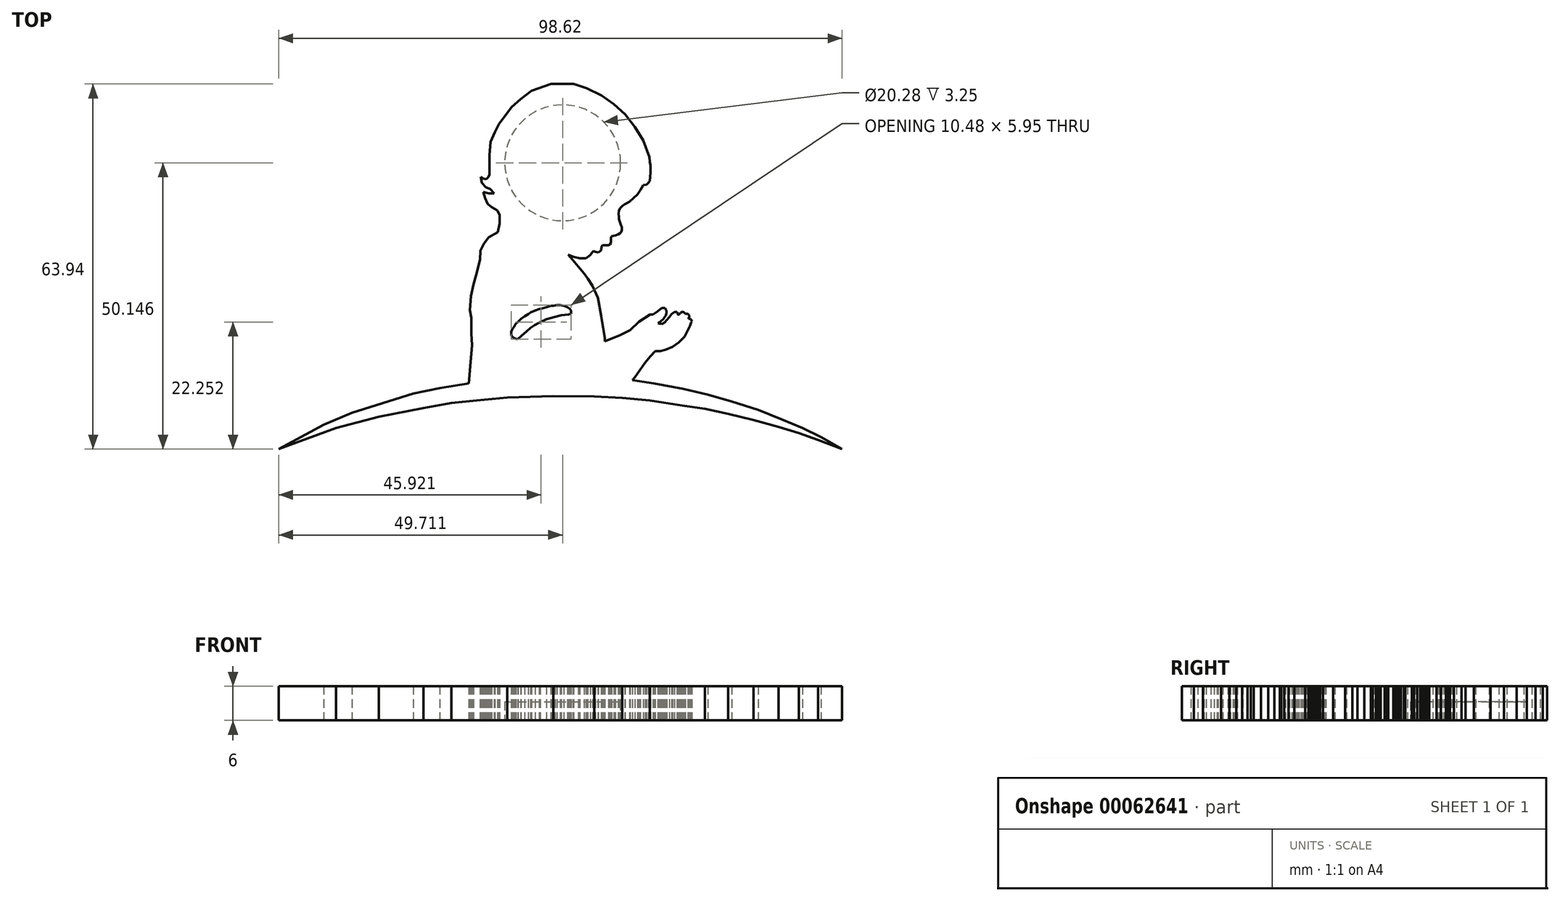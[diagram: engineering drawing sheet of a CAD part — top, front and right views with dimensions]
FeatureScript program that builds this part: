
annotation { "Feature Type Name" : "Feature", "Feature Type Description" : "" }
export const myFeature = defineFeature(function(context is Context, id is Id, definition is map)
    precondition{}
    {
        {
            var Q0;
            Q0=qCreatedBy(makeId("Top.planeOp"),FACE);
            var sketch = newSketch(context, id + "F0", { "sketchPlane" : qUnion([Q0])});
            skPoint(sketch, "E0", {"position": v(-48.76, -25.75) * mm});
            skPoint(sketch, "E1", {"position": v(-35.94, -19.4) * mm});
            skPoint(sketch, "E2", {"position": v(-15.46, -14.25) * mm});
            skPoint(sketch, "E3", {"position": v(-25.2, -16) * mm});
            skPoint(sketch, "E4", {"position": v(-15.02, -5.48) * mm});
            skPoint(sketch, "E5", {"position": v(-15.02, -2.75) * mm});
            skPoint(sketch, "E6", {"position": v(-13.48, 7.44) * mm});
            skPoint(sketch, "E7", {"position": v(-10.42, 12.26) * mm});
            skPoint(sketch, "E8", {"position": v(-12.94, 19.28) * mm});
            skPoint(sketch, "E9", {"position": v(-13.21, 20.85) * mm});
            skPoint(sketch, "E10", {"position": v(-12.46, 21.54) * mm});
            skPoint(sketch, "E11", {"position": v(-11.83, 22.37) * mm});
            skPoint(sketch, "E12", {"position": v(-10.23, 31.18) * mm});
            skPoint(sketch, "E13", {"position": v(-7.99, 34.13) * mm});
            skPoint(sketch, "E14", {"position": v(-4.5, 37) * mm});
            skPoint(sketch, "E15", {"position": v(-1.06, 38.2) * mm});
            skPoint(sketch, "E16", {"position": v(2.85, 38.2) * mm});
            skPoint(sketch, "E17", {"position": v(5.19, 37.46) * mm});
            skPoint(sketch, "E18", {"position": v(7.77, 36.2) * mm});
            skPoint(sketch, "E19", {"position": v(9.92, 34.68) * mm});
            skPoint(sketch, "E20", {"position": v(11.87, 32.87) * mm});
            skPoint(sketch, "E21", {"position": v(13.63, 30.68) * mm});
            skPoint(sketch, "E22", {"position": v(15.05, 28.34) * mm});
            skPoint(sketch, "E23", {"position": v(16.12, 25.36) * mm});
            skPoint(sketch, "E24", {"position": v(15.97, 20.87) * mm});
            skPoint(sketch, "E25", {"position": v(15.1, 20.48) * mm});
            skPoint(sketch, "E26", {"position": v(14.02, 18.87) * mm});
            skPoint(sketch, "E27", {"position": v(12.65, 17.55) * mm});
            skPoint(sketch, "E28", {"position": v(10.82, 16) * mm});
            skPoint(sketch, "E29", {"position": v(10.82, 14.53) * mm});
            skPoint(sketch, "E30", {"position": v(11.21, 13.4) * mm});
            skPoint(sketch, "E31", {"position": v(11.21, 12.27) * mm});
            skPoint(sketch, "E32", {"position": v(10.69, 11.83) * mm});
            skPoint(sketch, "E33", {"position": v(9.43, 11.31) * mm});
            skPoint(sketch, "E34", {"position": v(9.43, 10.4) * mm});
            skPoint(sketch, "E35", {"position": v(8.95, 9.96) * mm});
            skPoint(sketch, "E36", {"position": v(8.12, 9.96) * mm});
            skPoint(sketch, "E37", {"position": v(7.73, 9.1) * mm});
            skPoint(sketch, "E38", {"position": v(7.21, 8.7) * mm});
            skPoint(sketch, "E39", {"position": v(6.31, 8.93) * mm});
            skPoint(sketch, "E40", {"position": v(5.77, 8.25) * mm});
            skPoint(sketch, "E41", {"position": v(5.04, 7.66) * mm});
            skPoint(sketch, "E42", {"position": v(3.98, 7.66) * mm});
            skPoint(sketch, "E43", {"position": v(2.9, 7.92) * mm});
            skPoint(sketch, "E44", {"position": v(1.92, 8.33) * mm});
            skPoint(sketch, "E45", {"position": v(2.77, 7.38) * mm});
            skPoint(sketch, "E46", {"position": v(3.73, 6.24) * mm});
            skPoint(sketch, "E47", {"position": v(4.7, 5.02) * mm});
            skPoint(sketch, "E48", {"position": v(5.38, 4.1) * mm});
            skPoint(sketch, "E49", {"position": v(6.18, 2.85) * mm});
            skPoint(sketch, "E50", {"position": v(7.1, 0.73) * mm});
            skPoint(sketch, "E51", {"position": v(7.69, -2.44) * mm});
            skPoint(sketch, "E52", {"position": v(8.3, -6.28) * mm});
            skPoint(sketch, "E53", {"position": v(8.3, -6.86) * mm});
            skPoint(sketch, "E54", {"position": v(11.02, -5.81) * mm});
            skPoint(sketch, "E55", {"position": v(12.76, -4.93) * mm});
            skPoint(sketch, "E56", {"position": v(14.3, -3.45) * mm});
            skPoint(sketch, "E57", {"position": v(16.27, -2.2) * mm});
            skPoint(sketch, "E58", {"position": v(16.8, -2.2) * mm});
            skPoint(sketch, "E59", {"position": v(17.62, -1.58) * mm});
            skPoint(sketch, "E60", {"position": v(18.3, -1.02) * mm});
            skPoint(sketch, "E61", {"position": v(18.88, -1.02) * mm});
            skPoint(sketch, "E62", {"position": v(19.16, -1.52) * mm});
            skPoint(sketch, "E63", {"position": v(18.54, -3) * mm});
            skPoint(sketch, "E64", {"position": v(17.96, -3.48) * mm});
            skPoint(sketch, "E65", {"position": v(18.36, -3.8) * mm});
            skPoint(sketch, "E66", {"position": v(18.8, -3.54) * mm});
            skPoint(sketch, "E67", {"position": v(19.22, -3.14) * mm});
            skPoint(sketch, "E68", {"position": v(19.65, -2.62) * mm});
            skPoint(sketch, "E69", {"position": v(19.99, -2.1) * mm});
            skPoint(sketch, "E70", {"position": v(20.51, -1.73) * mm});
            skPoint(sketch, "E71", {"position": v(20.97, -1.73) * mm});
            skPoint(sketch, "E72", {"position": v(21.71, -1.8) * mm});
            skPoint(sketch, "E73", {"position": v(22.2, -1.8) * mm});
            skPoint(sketch, "E74", {"position": v(22.45, -2.04) * mm});
            skPoint(sketch, "E75", {"position": v(22.88, -2.04) * mm});
            skPoint(sketch, "E76", {"position": v(23.16, -2.38) * mm});
            skPoint(sketch, "E77", {"position": v(23.53, -3.2) * mm});
            skPoint(sketch, "E78", {"position": v(23.25, -4.11) * mm});
            skPoint(sketch, "E79", {"position": v(22.28, -6.06) * mm});
            skPoint(sketch, "E80", {"position": v(21.27, -7.08) * mm});
            skPoint(sketch, "E81", {"position": v(20.21, -7.84) * mm});
            skPoint(sketch, "E82", {"position": v(19, -8.34) * mm});
            skPoint(sketch, "E83", {"position": v(18.07, -8.57) * mm});
            skPoint(sketch, "E84", {"position": v(17.14, -8.57) * mm});
            skPoint(sketch, "E85", {"position": v(16.28, -9.55) * mm});
            skPoint(sketch, "E86", {"position": v(15.38, -10.65) * mm});
            skPoint(sketch, "E87", {"position": v(14.47, -11.9) * mm});
            skPoint(sketch, "E88", {"position": v(13.6, -13.17) * mm});
            skPoint(sketch, "E89", {"position": v(13.19, -13.66) * mm});
            skPoint(sketch, "E90", {"position": v(16.93, -14.2) * mm});
            skPoint(sketch, "E91", {"position": v(22.04, -15.17) * mm});
            skPoint(sketch, "E92", {"position": v(26.37, -16.18) * mm});
            skPoint(sketch, "E93", {"position": v(30.57, -17.38) * mm});
            skPoint(sketch, "E94", {"position": v(35.17, -18.86) * mm});
            skPoint(sketch, "E95", {"position": v(39.23, -20.51) * mm});
            skPoint(sketch, "E96", {"position": v(42.91, -22.04) * mm});
            skPoint(sketch, "E97", {"position": v(46.17, -23.61) * mm});
            skPoint(sketch, "E98", {"position": v(49.86, -25.75) * mm});
            skPoint(sketch, "E99", {"position": v(45.67, -24.16) * mm});
            skPoint(sketch, "E100", {"position": v(42.33, -22.95) * mm});
            skPoint(sketch, "E101", {"position": v(38.73, -21.84) * mm});
            skPoint(sketch, "E102", {"position": v(34.35, -20.64) * mm});
            skPoint(sketch, "E103", {"position": v(29.9, -19.56) * mm});
            skPoint(sketch, "E104", {"position": v(25.87, -18.7) * mm});
            skPoint(sketch, "E105", {"position": v(21.84, -18.08) * mm});
            skPoint(sketch, "E106", {"position": v(16.18, -17.23) * mm});
            skPoint(sketch, "E107", {"position": v(11.38, -16.77) * mm});
            skPoint(sketch, "E108", {"position": v(6.51, -16.53) * mm});
            skPoint(sketch, "E109", {"position": v(-0.71, -16.43) * mm});
            skPoint(sketch, "E110", {"position": v(-8.74, -16.74) * mm});
            skPoint(sketch, "E111", {"position": v(-14.08, -17.22) * mm});
            skPoint(sketch, "E112", {"position": v(-23.44, -18.54) * mm});
            skPoint(sketch, "E113", {"position": v(-18.54, -17.66) * mm});
            skPoint(sketch, "E114", {"position": v(-31.23, -20.1) * mm});
            skPoint(sketch, "E115", {"position": v(-38.75, -22.06) * mm});
            skPoint(sketch, "E116", {"position": v(-40.85, -21.47) * mm});
            skPoint(sketch, "E117", {"position": v(-20.59, -15.05) * mm});
            skPoint(sketch, "E118", {"position": v(-15.17, -10.5) * mm});
            skPoint(sketch, "E119", {"position": v(-14.93, -7.55) * mm});
            skPoint(sketch, "E120", {"position": v(-14.22, 4.7) * mm});
            skPoint(sketch, "E121", {"position": v(-15.27, -1.42) * mm});
            skPoint(sketch, "E122", {"position": v(-15.11, 1.1) * mm});
            skPoint(sketch, "E123", {"position": v(-14.62, 3.13) * mm});
            skPoint(sketch, "E124", {"position": v(-13.42, 9) * mm});
            skPoint(sketch, "E125", {"position": v(-12.84, 10.26) * mm});
            skPoint(sketch, "E126", {"position": v(-11.98, 11.34) * mm});
            skPoint(sketch, "E127", {"position": v(-10.07, 13.8) * mm});
            skPoint(sketch, "E128", {"position": v(-10.07, 15.24) * mm});
            skPoint(sketch, "E129", {"position": v(-10.46, 16.04) * mm});
            skPoint(sketch, "E130", {"position": v(-11.48, 16.6) * mm});
            skPoint(sketch, "E131", {"position": v(-12.2, 17.2) * mm});
            skPoint(sketch, "E132", {"position": v(-12.63, 18.2) * mm});
            skPoint(sketch, "E133", {"position": v(-12.01, 19.05) * mm});
            skPoint(sketch, "E134", {"position": v(-11.06, 19.05) * mm});
            skPoint(sketch, "E135", {"position": v(-11.7, 19.78) * mm});
            skPoint(sketch, "E136", {"position": v(-12.48, 20.14) * mm});
            skPoint(sketch, "E137", {"position": v(-13.38, 21.95) * mm});
            skPoint(sketch, "E138", {"position": v(-12.92, 21.66) * mm});
            skPoint(sketch, "E139", {"position": v(-12.04, 21.87) * mm});
            skPoint(sketch, "E140", {"position": v(-11.88, 25.7) * mm});
            skPoint(sketch, "E141", {"position": v(-11.64, 28.05) * mm});
            skPoint(sketch, "E142", {"position": v(-10.89, 29.8) * mm});
            skPoint(sketch, "E143", {"position": v(-6.42, 35.57) * mm});
            skPoint(sketch, "E144", {"position": v(-6.9, -6.47) * mm});
            skPoint(sketch, "E145", {"position": v(-6.19, -5.86) * mm});
            skPoint(sketch, "E146", {"position": v(-5.38, -5.16) * mm});
            skPoint(sketch, "E147", {"position": v(-4.68, -4.52) * mm});
            skPoint(sketch, "E148", {"position": v(-3.9, -4.03) * mm});
            skPoint(sketch, "E149", {"position": v(-3, -3.47) * mm});
            skPoint(sketch, "E150", {"position": v(-1.9, -3) * mm});
            skPoint(sketch, "E151", {"position": v(-0.5, -2.62) * mm});
            skPoint(sketch, "E152", {"position": v(0.72, -2.3) * mm});
            skPoint(sketch, "E153", {"position": v(1.99, -2.18) * mm});
            skPoint(sketch, "E154", {"position": v(2.4, -2.03) * mm});
            skPoint(sketch, "E155", {"position": v(2.4, -1.45) * mm});
            skPoint(sketch, "E156", {"position": v(2.16, -1.18) * mm});
            skPoint(sketch, "E157", {"position": v(1.8, -0.89) * mm});
            skPoint(sketch, "E158", {"position": v(1.18, -0.62) * mm});
            skPoint(sketch, "E159", {"position": v(0.5, -0.52) * mm});
            skPoint(sketch, "E160", {"position": v(-0.05, -0.52) * mm});
            skPoint(sketch, "E161", {"position": v(-0.7, -0.61) * mm});
            skPoint(sketch, "E162", {"position": v(-1.1, -0.67) * mm});
            skPoint(sketch, "E163", {"position": v(-1.7, -0.83) * mm});
            skPoint(sketch, "E164", {"position": v(-2.34, -1) * mm});
            skPoint(sketch, "E165", {"position": v(-4.59, -1.82) * mm});
            skPoint(sketch, "E166", {"position": v(-5.09, -2.1) * mm});
            skPoint(sketch, "E167", {"position": v(-5.72, -2.5) * mm});
            skPoint(sketch, "E168", {"position": v(-6.35, -2.96) * mm});
            skPoint(sketch, "E169", {"position": v(-6.84, -3.43) * mm});
            skPoint(sketch, "E170", {"position": v(-7.25, -3.85) * mm});
            skPoint(sketch, "E171", {"position": v(-7.56, -4.3) * mm});
            skPoint(sketch, "E172", {"position": v(-7.84, -4.72) * mm});
            skPoint(sketch, "E173", {"position": v(-8.08, -5.2) * mm});
            skPoint(sketch, "E174", {"position": v(-8.08, -5.66) * mm});
            skPoint(sketch, "E175", {"position": v(-7.96, -5.94) * mm});
            skPoint(sketch, "E176", {"position": v(-7.8, -6.1) * mm});
            skPoint(sketch, "E177", {"position": v(-7.56, -6.29) * mm});
            skPoint(sketch, "E178", {"position": v(-7.24, -6.45) * mm});
            skPoint(sketch, "E179", {"position": v(-3.87, -1.47) * mm});
            skPoint(sketch, "E180", {"position": v(-3.17, -1.22) * mm});
            skPoint(sketch, "E181", {"position": v(-0.38, -0.55) * mm});
            skLineSegment(sketch, "E182", {"start": v(-38.75, -22.06) * mm, "end": v(-48.76, -25.75) * mm});
            skLineSegment(sketch, "E183", {"start": v(-40.85, -21.47) * mm, "end": v(-35.94, -19.4) * mm});
            skLineSegment(sketch, "E184", {"start": v(-40.85, -21.47) * mm, "end": v(-48.76, -25.75) * mm});
            skLineSegment(sketch, "E185", {"start": v(-35.94, -19.4) * mm, "end": v(-25.2, -16) * mm});
            skLineSegment(sketch, "E186", {"start": v(-20.59, -15.05) * mm, "end": v(-25.2, -16) * mm});
            skLineSegment(sketch, "E187", {"start": v(-20.59, -15.05) * mm, "end": v(-15.46, -14.25) * mm});
            skLineSegment(sketch, "E188", {"start": v(-15.46, -14.25) * mm, "end": v(-15.17, -10.5) * mm});
            skLineSegment(sketch, "E189", {"start": v(-15.17, -10.5) * mm, "end": v(-14.93, -7.55) * mm});
            skLineSegment(sketch, "E190", {"start": v(-15.02, -5.48) * mm, "end": v(-14.93, -7.55) * mm});
            skLineSegment(sketch, "E191", {"start": v(-15.02, -5.48) * mm, "end": v(-15.02, -2.75) * mm});
            skLineSegment(sketch, "E192", {"start": v(-15.02, -2.75) * mm, "end": v(-15.27, -1.42) * mm});
            skLineSegment(sketch, "E193", {"start": v(-15.27, -1.42) * mm, "end": v(-15.11, 1.1) * mm});
            skLineSegment(sketch, "E194", {"start": v(-15.11, 1.1) * mm, "end": v(-14.62, 3.13) * mm});
            skLineSegment(sketch, "E195", {"start": v(-14.62, 3.13) * mm, "end": v(-14.22, 4.7) * mm});
            skLineSegment(sketch, "E196", {"start": v(-14.22, 4.7) * mm, "end": v(-13.48, 7.44) * mm});
            skLineSegment(sketch, "E197", {"start": v(-13.48, 7.44) * mm, "end": v(-13.42, 9) * mm});
            skLineSegment(sketch, "E198", {"start": v(-13.42, 9) * mm, "end": v(-12.84, 10.26) * mm});
            skLineSegment(sketch, "E199", {"start": v(-12.84, 10.26) * mm, "end": v(-11.98, 11.34) * mm});
            skLineSegment(sketch, "E200", {"start": v(-11.98, 11.34) * mm, "end": v(-10.42, 12.26) * mm});
            skLineSegment(sketch, "E201", {"start": v(-10.42, 12.26) * mm, "end": v(-10.07, 13.8) * mm});
            skLineSegment(sketch, "E202", {"start": v(-10.46, 16.04) * mm, "end": v(-10.07, 15.24) * mm});
            skLineSegment(sketch, "E203", {"start": v(-10.46, 16.04) * mm, "end": v(-11.48, 16.6) * mm});
            skLineSegment(sketch, "E204", {"start": v(-11.48, 16.6) * mm, "end": v(-12.2, 17.2) * mm});
            skLineSegment(sketch, "E205", {"start": v(-12.2, 17.2) * mm, "end": v(-12.63, 18.2) * mm});
            skLineSegment(sketch, "E206", {"start": v(-12.63, 18.2) * mm, "end": v(-12.94, 19.28) * mm});
            skLineSegment(sketch, "E207", {"start": v(-12.01, 19.05) * mm, "end": v(-12.94, 19.28) * mm});
            skLineSegment(sketch, "E208", {"start": v(-12.01, 19.05) * mm, "end": v(-11.06, 19.05) * mm});
            skLineSegment(sketch, "E209", {"start": v(-11.7, 19.78) * mm, "end": v(-11.06, 19.05) * mm});
            skLineSegment(sketch, "E210", {"start": v(-11.7, 19.78) * mm, "end": v(-12.48, 20.14) * mm});
            skLineSegment(sketch, "E211", {"start": v(-12.48, 20.14) * mm, "end": v(-13.21, 20.85) * mm});
            skLineSegment(sketch, "E212", {"start": v(-13.21, 20.85) * mm, "end": v(-13.38, 21.95) * mm});
            skLineSegment(sketch, "E213", {"start": v(-13.38, 21.95) * mm, "end": v(-12.92, 21.66) * mm});
            skLineSegment(sketch, "E214", {"start": v(-12.92, 21.66) * mm, "end": v(-12.46, 21.54) * mm});
            skLineSegment(sketch, "E215", {"start": v(-12.46, 21.54) * mm, "end": v(-12.04, 21.87) * mm});
            skLineSegment(sketch, "E216", {"start": v(-12.04, 21.87) * mm, "end": v(-11.83, 22.37) * mm});
            skLineSegment(sketch, "E217", {"start": v(-11.83, 22.37) * mm, "end": v(-11.88, 25.7) * mm});
            skLineSegment(sketch, "E218", {"start": v(-11.88, 25.7) * mm, "end": v(-11.64, 28.05) * mm});
            skLineSegment(sketch, "E219", {"start": v(-11.64, 28.05) * mm, "end": v(-10.89, 29.8) * mm});
            skLineSegment(sketch, "E220", {"start": v(-10.89, 29.8) * mm, "end": v(-10.23, 31.18) * mm});
            skLineSegment(sketch, "E221", {"start": v(-10.23, 31.18) * mm, "end": v(-7.99, 34.13) * mm});
            skLineSegment(sketch, "E222", {"start": v(-7.99, 34.13) * mm, "end": v(-6.42, 35.57) * mm});
            skLineSegment(sketch, "E223", {"start": v(-6.42, 35.57) * mm, "end": v(-4.5, 37) * mm});
            skLineSegment(sketch, "E224", {"start": v(-4.5, 37) * mm, "end": v(-1.06, 38.2) * mm});
            skLineSegment(sketch, "E225", {"start": v(-1.06, 38.2) * mm, "end": v(2.85, 38.2) * mm});
            skLineSegment(sketch, "E226", {"start": v(2.85, 38.2) * mm, "end": v(5.19, 37.46) * mm});
            skLineSegment(sketch, "E227", {"start": v(5.19, 37.46) * mm, "end": v(7.77, 36.2) * mm});
            skLineSegment(sketch, "E228", {"start": v(7.77, 36.2) * mm, "end": v(9.92, 34.68) * mm});
            skLineSegment(sketch, "E229", {"start": v(9.92, 34.68) * mm, "end": v(11.87, 32.87) * mm});
            skLineSegment(sketch, "E230", {"start": v(11.87, 32.87) * mm, "end": v(13.63, 30.68) * mm});
            skLineSegment(sketch, "E231", {"start": v(13.63, 30.68) * mm, "end": v(15.05, 28.34) * mm});
            skLineSegment(sketch, "E232", {"start": v(15.05, 28.34) * mm, "end": v(16.12, 25.36) * mm});
            skPoint(sketch, "E233", {"position": v(16.23, 24.57) * mm});
            skPoint(sketch, "E234", {"position": v(16.31, 23.9) * mm});
            skPoint(sketch, "E235", {"position": v(16.31, 22.72) * mm});
            skPoint(sketch, "E236", {"position": v(16.28, 21.89) * mm});
            skPoint(sketch, "E237", {"position": v(16.23, 21.2) * mm});
            skPoint(sketch, "E238", {"position": v(15.62, 20.58) * mm});
            skPoint(sketch, "E239", {"position": v(14.56, 19.63) * mm});
            skLineSegment(sketch, "E240", {"start": v(16.12, 25.36) * mm, "end": v(16.23, 24.57) * mm});
            skLineSegment(sketch, "E241", {"start": v(16.23, 24.57) * mm, "end": v(16.31, 23.9) * mm});
            skLineSegment(sketch, "E242", {"start": v(16.28, 21.89) * mm, "end": v(16.31, 22.72) * mm});
            skLineSegment(sketch, "E243", {"start": v(16.28, 21.89) * mm, "end": v(16.23, 21.2) * mm});
            skLineSegment(sketch, "E244", {"start": v(16.23, 21.2) * mm, "end": v(15.97, 20.87) * mm});
            skLineSegment(sketch, "E245", {"start": v(15.97, 20.87) * mm, "end": v(15.62, 20.58) * mm});
            skLineSegment(sketch, "E246", {"start": v(15.62, 20.58) * mm, "end": v(15.1, 20.48) * mm});
            skLineSegment(sketch, "E247", {"start": v(15.1, 20.48) * mm, "end": v(14.56, 19.63) * mm});
            skLineSegment(sketch, "E248", {"start": v(14.56, 19.63) * mm, "end": v(14.02, 18.87) * mm});
            skLineSegment(sketch, "E249", {"start": v(14.02, 18.87) * mm, "end": v(12.65, 17.55) * mm});
            skPoint(sketch, "E250", {"position": v(11.84, 17.1) * mm});
            skPoint(sketch, "E251", {"position": v(11.39, 16.83) * mm});
            skPoint(sketch, "E252", {"position": v(11.02, 16.42) * mm});
            skLineSegment(sketch, "E253", {"start": v(12.65, 17.55) * mm, "end": v(11.84, 17.1) * mm});
            skLineSegment(sketch, "E254", {"start": v(11.84, 17.1) * mm, "end": v(11.39, 16.83) * mm});
            skLineSegment(sketch, "E255", {"start": v(11.39, 16.83) * mm, "end": v(11.02, 16.42) * mm});
            skLineSegment(sketch, "E256", {"start": v(11.02, 16.42) * mm, "end": v(10.82, 16) * mm});
            skPoint(sketch, "E257", {"position": v(10.73, 15.5) * mm});
            skPoint(sketch, "E258", {"position": v(10.8, 14.9) * mm});
            skLineSegment(sketch, "E259", {"start": v(10.82, 16) * mm, "end": v(10.73, 15.5) * mm});
            skLineSegment(sketch, "E260", {"start": v(10.73, 15.5) * mm, "end": v(10.8, 14.9) * mm});
            skLineSegment(sketch, "E261", {"start": v(10.8, 14.9) * mm, "end": v(10.82, 14.53) * mm});
            skLineSegment(sketch, "E262", {"start": v(10.82, 14.53) * mm, "end": v(11.21, 13.4) * mm});
            skPoint(sketch, "E263", {"position": v(11.3, 13.14) * mm});
            skPoint(sketch, "E264", {"position": v(11.32, 12.6) * mm});
            skPoint(sketch, "E265", {"position": v(10.98, 12.03) * mm});
            skPoint(sketch, "E266", {"position": v(10.15, 11.65) * mm});
            skPoint(sketch, "E267", {"position": v(9.51, 11.57) * mm});
            skLineSegment(sketch, "E268", {"start": v(11.21, 13.4) * mm, "end": v(11.3, 13.14) * mm});
            skLineSegment(sketch, "E269", {"start": v(11.3, 13.14) * mm, "end": v(11.32, 12.6) * mm});
            skLineSegment(sketch, "E270", {"start": v(11.32, 12.6) * mm, "end": v(11.21, 12.27) * mm});
            skLineSegment(sketch, "E271", {"start": v(11.21, 12.27) * mm, "end": v(10.98, 12.03) * mm});
            skLineSegment(sketch, "E272", {"start": v(10.98, 12.03) * mm, "end": v(10.69, 11.83) * mm});
            skLineSegment(sketch, "E273", {"start": v(10.69, 11.83) * mm, "end": v(10.15, 11.65) * mm});
            skLineSegment(sketch, "E274", {"start": v(10.15, 11.65) * mm, "end": v(9.51, 11.57) * mm});
            skLineSegment(sketch, "E275", {"start": v(9.51, 11.57) * mm, "end": v(9.43, 11.31) * mm});
            skLineSegment(sketch, "E276", {"start": v(9.43, 11.31) * mm, "end": v(9.43, 10.4) * mm});
            skPoint(sketch, "E277", {"position": v(9.24, 10.08) * mm});
            skLineSegment(sketch, "E278", {"start": v(9.43, 10.4) * mm, "end": v(9.24, 10.08) * mm});
            skLineSegment(sketch, "E279", {"start": v(9.24, 10.08) * mm, "end": v(8.95, 9.96) * mm});
            skLineSegment(sketch, "E280", {"start": v(8.95, 9.96) * mm, "end": v(8.12, 9.96) * mm});
            skPoint(sketch, "E281", {"position": v(7.94, 9.94) * mm});
            skPoint(sketch, "E282", {"position": v(7.78, 9.77) * mm});
            skLineSegment(sketch, "E283", {"start": v(8.12, 9.96) * mm, "end": v(7.94, 9.94) * mm});
            skLineSegment(sketch, "E284", {"start": v(7.94, 9.94) * mm, "end": v(7.78, 9.77) * mm});
            skLineSegment(sketch, "E285", {"start": v(7.78, 9.77) * mm, "end": v(7.73, 9.1) * mm});
            skLineSegment(sketch, "E286", {"start": v(7.73, 9.1) * mm, "end": v(7.21, 8.7) * mm});
            skLineSegment(sketch, "E287", {"start": v(7.21, 8.7) * mm, "end": v(6.7, 8.84) * mm});
            skLineSegment(sketch, "E288", {"start": v(6.7, 8.84) * mm, "end": v(6.31, 8.93) * mm});
            skLineSegment(sketch, "E289", {"start": v(6.31, 8.93) * mm, "end": v(5.77, 8.25) * mm});
            skLineSegment(sketch, "E290", {"start": v(5.77, 8.25) * mm, "end": v(5.04, 7.66) * mm});
            skLineSegment(sketch, "E291", {"start": v(5.04, 7.66) * mm, "end": v(3.98, 7.66) * mm});
            skLineSegment(sketch, "E292", {"start": v(3.98, 7.66) * mm, "end": v(2.9, 7.92) * mm});
            skLineSegment(sketch, "E293", {"start": v(2.9, 7.92) * mm, "end": v(1.92, 8.33) * mm});
            skLineSegment(sketch, "E294", {"start": v(1.92, 8.33) * mm, "end": v(2.77, 7.38) * mm});
            skLineSegment(sketch, "E295", {"start": v(2.77, 7.38) * mm, "end": v(3.73, 6.24) * mm});
            skLineSegment(sketch, "E296", {"start": v(3.73, 6.24) * mm, "end": v(4.7, 5.02) * mm});
            skLineSegment(sketch, "E297", {"start": v(4.7, 5.02) * mm, "end": v(5.38, 4.1) * mm});
            skLineSegment(sketch, "E298", {"start": v(5.38, 4.1) * mm, "end": v(6.18, 2.85) * mm});
            skLineSegment(sketch, "E299", {"start": v(6.18, 2.85) * mm, "end": v(7.1, 0.73) * mm});
            skLineSegment(sketch, "E300", {"start": v(7.1, 0.73) * mm, "end": v(7.69, -2.44) * mm});
            skLineSegment(sketch, "E301", {"start": v(7.69, -2.44) * mm, "end": v(8.3, -6.28) * mm});
            skLineSegment(sketch, "E302", {"start": v(8.3, -6.28) * mm, "end": v(8.3, -6.86) * mm});
            skLineSegment(sketch, "E303", {"start": v(8.3, -6.86) * mm, "end": v(11.02, -5.81) * mm});
            skLineSegment(sketch, "E304", {"start": v(11.02, -5.81) * mm, "end": v(12.76, -4.93) * mm});
            skLineSegment(sketch, "E305", {"start": v(12.76, -4.93) * mm, "end": v(14.3, -3.45) * mm});
            skLineSegment(sketch, "E306", {"start": v(14.3, -3.45) * mm, "end": v(16.27, -2.2) * mm});
            skLineSegment(sketch, "E307", {"start": v(16.27, -2.2) * mm, "end": v(16.8, -2.2) * mm});
            skLineSegment(sketch, "E308", {"start": v(16.8, -2.2) * mm, "end": v(17.62, -1.58) * mm});
            skLineSegment(sketch, "E309", {"start": v(17.62, -1.58) * mm, "end": v(18.3, -1.02) * mm});
            skLineSegment(sketch, "E310", {"start": v(18.3, -1.02) * mm, "end": v(18.88, -1.02) * mm});
            skLineSegment(sketch, "E311", {"start": v(18.88, -1.02) * mm, "end": v(19.16, -1.52) * mm});
            skPoint(sketch, "E312", {"position": v(19.13, -1.89) * mm});
            skPoint(sketch, "E313", {"position": v(19.08, -2.15) * mm});
            skPoint(sketch, "E314", {"position": v(18.98, -2.37) * mm});
            skPoint(sketch, "E315", {"position": v(18.84, -2.6) * mm});
            skPoint(sketch, "E316", {"position": v(18.7, -2.83) * mm});
            skPoint(sketch, "E317", {"position": v(18.26, -3.27) * mm});
            skLineSegment(sketch, "E318", {"start": v(19.16, -1.52) * mm, "end": v(19.13, -1.89) * mm});
            skLineSegment(sketch, "E319", {"start": v(19.13, -1.89) * mm, "end": v(19.08, -2.15) * mm});
            skLineSegment(sketch, "E320", {"start": v(19.08, -2.15) * mm, "end": v(18.98, -2.37) * mm});
            skLineSegment(sketch, "E321", {"start": v(18.98, -2.37) * mm, "end": v(18.84, -2.6) * mm});
            skLineSegment(sketch, "E322", {"start": v(18.84, -2.6) * mm, "end": v(18.7, -2.83) * mm});
            skLineSegment(sketch, "E323", {"start": v(18.7, -2.83) * mm, "end": v(18.54, -3) * mm});
            skLineSegment(sketch, "E324", {"start": v(18.54, -3) * mm, "end": v(18.26, -3.27) * mm});
            skLineSegment(sketch, "E325", {"start": v(18.26, -3.27) * mm, "end": v(17.96, -3.48) * mm});
            skPoint(sketch, "E326", {"position": v(17.81, -3.6) * mm});
            skPoint(sketch, "E327", {"position": v(17.67, -3.69) * mm});
            skPoint(sketch, "E328", {"position": v(17.83, -3.75) * mm});
            skLineSegment(sketch, "E329", {"start": v(17.96, -3.48) * mm, "end": v(17.81, -3.6) * mm});
            skLineSegment(sketch, "E330", {"start": v(17.81, -3.6) * mm, "end": v(17.67, -3.69) * mm});
            skLineSegment(sketch, "E331", {"start": v(17.67, -3.69) * mm, "end": v(17.83, -3.75) * mm});
            skLineSegment(sketch, "E332", {"start": v(17.83, -3.75) * mm, "end": v(18.36, -3.8) * mm});
            skLineSegment(sketch, "E333", {"start": v(18.36, -3.8) * mm, "end": v(18.8, -3.54) * mm});
            skLineSegment(sketch, "E334", {"start": v(18.8, -3.54) * mm, "end": v(19.22, -3.14) * mm});
            skLineSegment(sketch, "E335", {"start": v(19.22, -3.14) * mm, "end": v(19.65, -2.62) * mm});
            skLineSegment(sketch, "E336", {"start": v(19.65, -2.62) * mm, "end": v(19.99, -2.1) * mm});
            skLineSegment(sketch, "E337", {"start": v(19.99, -2.1) * mm, "end": v(20.51, -1.73) * mm});
            skLineSegment(sketch, "E338", {"start": v(20.51, -1.73) * mm, "end": v(20.97, -1.73) * mm});
            skPoint(sketch, "E339", {"position": v(21.05, -1.84) * mm});
            skPoint(sketch, "E340", {"position": v(21.12, -2) * mm});
            skPoint(sketch, "E341", {"position": v(21.16, -2.18) * mm});
            skPoint(sketch, "E342", {"position": v(21.18, -2.3) * mm});
            skPoint(sketch, "E343", {"position": v(21.3, -2.19) * mm});
            skPoint(sketch, "E344", {"position": v(21.42, -2.06) * mm});
            skPoint(sketch, "E345", {"position": v(21.54, -1.97) * mm});
            skPoint(sketch, "E346", {"position": v(21.62, -1.87) * mm});
            skPoint(sketch, "E347", {"position": v(21.87, -1.75) * mm});
            skPoint(sketch, "E348", {"position": v(22.02, -1.73) * mm});
            skLineSegment(sketch, "E349", {"start": v(20.97, -1.73) * mm, "end": v(21.05, -1.84) * mm});
            skLineSegment(sketch, "E350", {"start": v(21.05, -1.84) * mm, "end": v(21.12, -2) * mm});
            skLineSegment(sketch, "E351", {"start": v(21.12, -2) * mm, "end": v(21.16, -2.18) * mm});
            skLineSegment(sketch, "E352", {"start": v(21.16, -2.22) * mm, "end": v(21.18, -2.3) * mm});
            skLineSegment(sketch, "E353", {"start": v(21.16, -2.22) * mm, "end": v(21.16, -2.18) * mm});
            skLineSegment(sketch, "E354", {"start": v(21.18, -2.3) * mm, "end": v(21.3, -2.19) * mm});
            skLineSegment(sketch, "E355", {"start": v(21.3, -2.19) * mm, "end": v(21.42, -2.06) * mm});
            skLineSegment(sketch, "E356", {"start": v(21.42, -2.06) * mm, "end": v(21.54, -1.97) * mm});
            skLineSegment(sketch, "E357", {"start": v(21.54, -1.97) * mm, "end": v(21.62, -1.87) * mm});
            skLineSegment(sketch, "E358", {"start": v(21.62, -1.87) * mm, "end": v(21.71, -1.8) * mm});
            skLineSegment(sketch, "E359", {"start": v(21.71, -1.8) * mm, "end": v(21.87, -1.75) * mm});
            skLineSegment(sketch, "E360", {"start": v(21.87, -1.75) * mm, "end": v(22.02, -1.73) * mm});
            skLineSegment(sketch, "E361", {"start": v(22.02, -1.73) * mm, "end": v(22.2, -1.8) * mm});
            skLineSegment(sketch, "E362", {"start": v(22.2, -1.8) * mm, "end": v(22.45, -2.04) * mm});
            skLineSegment(sketch, "E363", {"start": v(22.45, -2.04) * mm, "end": v(22.88, -2.04) * mm});
            skLineSegment(sketch, "E364", {"start": v(23.16, -2.38) * mm, "end": v(22.88, -2.04) * mm});
            skPoint(sketch, "E365", {"position": v(23.15, -2.53) * mm});
            skPoint(sketch, "E366", {"position": v(23.08, -2.68) * mm});
            skPoint(sketch, "E367", {"position": v(23, -2.8) * mm});
            skPoint(sketch, "E368", {"position": v(23.02, -2.94) * mm});
            skPoint(sketch, "E369", {"position": v(23.3, -2.95) * mm});
            skPoint(sketch, "E370", {"position": v(23.44, -3.04) * mm});
            skPoint(sketch, "E371", {"position": v(23.57, -3.36) * mm});
            skPoint(sketch, "E372", {"position": v(23.47, -3.55) * mm});
            skLineSegment(sketch, "E373", {"start": v(23.16, -2.38) * mm, "end": v(23.15, -2.53) * mm});
            skLineSegment(sketch, "E374", {"start": v(23.15, -2.53) * mm, "end": v(23.08, -2.68) * mm});
            skLineSegment(sketch, "E375", {"start": v(23.08, -2.68) * mm, "end": v(23, -2.8) * mm});
            skLineSegment(sketch, "E376", {"start": v(23, -2.8) * mm, "end": v(23.02, -2.94) * mm});
            skLineSegment(sketch, "E377", {"start": v(23.02, -2.94) * mm, "end": v(23.3, -2.95) * mm});
            skLineSegment(sketch, "E378", {"start": v(23.3, -2.95) * mm, "end": v(23.44, -3.04) * mm});
            skLineSegment(sketch, "E379", {"start": v(23.44, -3.04) * mm, "end": v(23.53, -3.2) * mm});
            skLineSegment(sketch, "E380", {"start": v(23.53, -3.2) * mm, "end": v(23.57, -3.36) * mm});
            skLineSegment(sketch, "E381", {"start": v(23.57, -3.36) * mm, "end": v(23.47, -3.55) * mm});
            skLineSegment(sketch, "E382", {"start": v(23.47, -3.55) * mm, "end": v(23.25, -4.11) * mm});
            skLineSegment(sketch, "E383", {"start": v(23.25, -4.11) * mm, "end": v(22.28, -6.06) * mm});
            skLineSegment(sketch, "E384", {"start": v(22.28, -6.06) * mm, "end": v(21.27, -7.08) * mm});
            skLineSegment(sketch, "E385", {"start": v(21.27, -7.08) * mm, "end": v(20.21, -7.84) * mm});
            skLineSegment(sketch, "E386", {"start": v(20.21, -7.84) * mm, "end": v(19, -8.34) * mm});
            skLineSegment(sketch, "E387", {"start": v(19, -8.34) * mm, "end": v(18.07, -8.57) * mm});
            skLineSegment(sketch, "E388", {"start": v(18.07, -8.57) * mm, "end": v(17.14, -8.57) * mm});
            skLineSegment(sketch, "E389", {"start": v(17.14, -8.57) * mm, "end": v(16.28, -9.55) * mm});
            skLineSegment(sketch, "E390", {"start": v(16.28, -9.55) * mm, "end": v(15.38, -10.65) * mm});
            skLineSegment(sketch, "E391", {"start": v(15.38, -10.65) * mm, "end": v(14.47, -11.9) * mm});
            skLineSegment(sketch, "E392", {"start": v(14.47, -11.9) * mm, "end": v(13.6, -13.17) * mm});
            skLineSegment(sketch, "E393", {"start": v(13.6, -13.17) * mm, "end": v(13.19, -13.66) * mm});
            skLineSegment(sketch, "E394", {"start": v(13.19, -13.66) * mm, "end": v(16.93, -14.2) * mm});
            skLineSegment(sketch, "E395", {"start": v(16.93, -14.2) * mm, "end": v(22.04, -15.17) * mm});
            skLineSegment(sketch, "E396", {"start": v(22.04, -15.17) * mm, "end": v(26.37, -16.18) * mm});
            skLineSegment(sketch, "E397", {"start": v(26.37, -16.18) * mm, "end": v(30.57, -17.38) * mm});
            skLineSegment(sketch, "E398", {"start": v(30.57, -17.38) * mm, "end": v(35.17, -18.86) * mm});
            skLineSegment(sketch, "E399", {"start": v(35.17, -18.86) * mm, "end": v(39.23, -20.51) * mm});
            skLineSegment(sketch, "E400", {"start": v(39.23, -20.51) * mm, "end": v(42.91, -22.04) * mm});
            skLineSegment(sketch, "E401", {"start": v(42.91, -22.04) * mm, "end": v(46.17, -23.61) * mm});
            skLineSegment(sketch, "E402", {"start": v(46.17, -23.61) * mm, "end": v(49.86, -25.75) * mm});
            skLineSegment(sketch, "E403", {"start": v(49.86, -25.75) * mm, "end": v(45.67, -24.16) * mm});
            skLineSegment(sketch, "E404", {"start": v(45.67, -24.16) * mm, "end": v(42.33, -22.95) * mm});
            skLineSegment(sketch, "E405", {"start": v(42.33, -22.95) * mm, "end": v(38.73, -21.84) * mm});
            skLineSegment(sketch, "E406", {"start": v(38.73, -21.84) * mm, "end": v(34.35, -20.64) * mm});
            skLineSegment(sketch, "E407", {"start": v(34.35, -20.64) * mm, "end": v(29.9, -19.56) * mm});
            skLineSegment(sketch, "E408", {"start": v(29.9, -19.56) * mm, "end": v(25.87, -18.7) * mm});
            skLineSegment(sketch, "E409", {"start": v(25.87, -18.7) * mm, "end": v(21.84, -18.08) * mm});
            skLineSegment(sketch, "E410", {"start": v(21.84, -18.08) * mm, "end": v(16.18, -17.23) * mm});
            skLineSegment(sketch, "E411", {"start": v(16.18, -17.23) * mm, "end": v(11.38, -16.77) * mm});
            skLineSegment(sketch, "E412", {"start": v(11.38, -16.77) * mm, "end": v(6.51, -16.53) * mm});
            skLineSegment(sketch, "E413", {"start": v(6.51, -16.53) * mm, "end": v(-0.71, -16.43) * mm});
            skLineSegment(sketch, "E414", {"start": v(-0.71, -16.43) * mm, "end": v(-8.74, -16.74) * mm});
            skLineSegment(sketch, "E415", {"start": v(-8.74, -16.74) * mm, "end": v(-14.08, -17.22) * mm});
            skLineSegment(sketch, "E416", {"start": v(-14.08, -17.22) * mm, "end": v(-18.54, -17.66) * mm});
            skLineSegment(sketch, "E417", {"start": v(-18.54, -17.66) * mm, "end": v(-23.44, -18.54) * mm});
            skLineSegment(sketch, "E418", {"start": v(-23.44, -18.54) * mm, "end": v(-31.23, -20.1) * mm});
            skLineSegment(sketch, "E419", {"start": v(-31.23, -20.1) * mm, "end": v(-38.75, -22.06) * mm});
            skLineSegment(sketch, "E420", {"start": v(0.72, -2.3) * mm, "end": v(1.99, -2.18) * mm});
            skLineSegment(sketch, "E421", {"start": v(1.99, -2.18) * mm, "end": v(2.4, -2.03) * mm});
            skLineSegment(sketch, "E422", {"start": v(2.4, -2.03) * mm, "end": v(2.4, -1.45) * mm});
            skLineSegment(sketch, "E423", {"start": v(2.4, -1.45) * mm, "end": v(2.16, -1.18) * mm});
            skLineSegment(sketch, "E424", {"start": v(2.16, -1.18) * mm, "end": v(1.8, -0.89) * mm});
            skLineSegment(sketch, "E425", {"start": v(1.8, -0.89) * mm, "end": v(1.18, -0.62) * mm});
            skLineSegment(sketch, "E426", {"start": v(1.18, -0.62) * mm, "end": v(0.5, -0.52) * mm});
            skLineSegment(sketch, "E427", {"start": v(0.5, -0.52) * mm, "end": v(-0.05, -0.52) * mm});
            skLineSegment(sketch, "E428", {"start": v(-0.05, -0.52) * mm, "end": v(-0.38, -0.55) * mm});
            skLineSegment(sketch, "E429", {"start": v(-0.38, -0.55) * mm, "end": v(-0.7, -0.61) * mm});
            skLineSegment(sketch, "E430", {"start": v(-0.7, -0.61) * mm, "end": v(-1.1, -0.67) * mm});
            skLineSegment(sketch, "E431", {"start": v(-1.1, -0.67) * mm, "end": v(-1.7, -0.83) * mm});
            skLineSegment(sketch, "E432", {"start": v(-1.7, -0.83) * mm, "end": v(-2.34, -1) * mm});
            skLineSegment(sketch, "E433", {"start": v(-2.34, -1) * mm, "end": v(-3.17, -1.22) * mm});
            skLineSegment(sketch, "E434", {"start": v(-3.17, -1.22) * mm, "end": v(-3.87, -1.47) * mm});
            skLineSegment(sketch, "E435", {"start": v(-3.87, -1.47) * mm, "end": v(-4.59, -1.82) * mm});
            skLineSegment(sketch, "E436", {"start": v(-4.59, -1.82) * mm, "end": v(-5.09, -2.1) * mm});
            skLineSegment(sketch, "E437", {"start": v(-5.09, -2.1) * mm, "end": v(-5.72, -2.5) * mm});
            skLineSegment(sketch, "E438", {"start": v(-5.72, -2.5) * mm, "end": v(-6.35, -2.96) * mm});
            skLineSegment(sketch, "E439", {"start": v(-6.35, -2.96) * mm, "end": v(-6.84, -3.43) * mm});
            skLineSegment(sketch, "E440", {"start": v(-6.84, -3.43) * mm, "end": v(-7.25, -3.85) * mm});
            skLineSegment(sketch, "E441", {"start": v(-7.25, -3.85) * mm, "end": v(-7.56, -4.3) * mm});
            skLineSegment(sketch, "E442", {"start": v(-7.56, -4.3) * mm, "end": v(-7.84, -4.72) * mm});
            skLineSegment(sketch, "E443", {"start": v(-7.84, -4.72) * mm, "end": v(-8.08, -5.2) * mm});
            skLineSegment(sketch, "E444", {"start": v(-8.08, -5.2) * mm, "end": v(-8.08, -5.66) * mm});
            skLineSegment(sketch, "E445", {"start": v(-8.08, -5.66) * mm, "end": v(-7.96, -5.94) * mm});
            skLineSegment(sketch, "E446", {"start": v(-7.96, -5.94) * mm, "end": v(-7.8, -6.1) * mm});
            skLineSegment(sketch, "E447", {"start": v(-7.8, -6.1) * mm, "end": v(-7.56, -6.29) * mm});
            skLineSegment(sketch, "E448", {"start": v(-7.56, -6.29) * mm, "end": v(-7.24, -6.45) * mm});
            skLineSegment(sketch, "E449", {"start": v(-7.24, -6.45) * mm, "end": v(-6.9, -6.47) * mm});
            skLineSegment(sketch, "E450", {"start": v(-6.9, -6.47) * mm, "end": v(-6.19, -5.86) * mm});
            skLineSegment(sketch, "E451", {"start": v(-6.19, -5.86) * mm, "end": v(-5.38, -5.16) * mm});
            skLineSegment(sketch, "E452", {"start": v(-5.38, -5.16) * mm, "end": v(-4.68, -4.52) * mm});
            skLineSegment(sketch, "E453", {"start": v(-4.68, -4.52) * mm, "end": v(-3.9, -4.03) * mm});
            skLineSegment(sketch, "E454", {"start": v(-3.9, -4.03) * mm, "end": v(-3, -3.47) * mm});
            skLineSegment(sketch, "E455", {"start": v(-3, -3.47) * mm, "end": v(-1.9, -3) * mm});
            skLineSegment(sketch, "E456", {"start": v(-1.9, -3) * mm, "end": v(-0.5, -2.62) * mm});
            skLineSegment(sketch, "E457", {"start": v(-0.5, -2.62) * mm, "end": v(0.72, -2.3) * mm});
            skPoint(sketch, "E458", {"position": v(16.33, 23.2) * mm});
            skLineSegment(sketch, "E459", {"start": v(16.31, 22.72) * mm, "end": v(16.33, 23.2) * mm});
            skLineSegment(sketch, "E460", {"start": v(16.33, 23.2) * mm, "end": v(16.31, 23.9) * mm});
            skLineSegment(sketch, "E461", {"start": v(-10.07, 15.24) * mm, "end": v(-10.07, 13.8) * mm});
            skLineSegment(sketch, "E462.bottom", {"start": v(-65.5, 51.04) * mm, "end": v(68.6, 51.04) * mm});
            skLineSegment(sketch, "E462.top", {"start": v(-65.5, -46.26) * mm, "end": v(68.6, -46.26) * mm});
            skLineSegment(sketch, "E462.left", {"start": v(-65.5, 51.04) * mm, "end": v(-65.5, -46.26) * mm});
            skLineSegment(sketch, "E462.right", {"start": v(68.6, 51.04) * mm, "end": v(68.6, -46.26) * mm});
            skSolve(sketch);
        }
        {
            var Q0;
            Q0=makeQuery(id+"F0.imprint","IMPRINT",FACE,{"disambiguationData":[TD([[makeQuery(id+"F0.imprint","IMPRINT",EDGE,{"derivedFrom":sQuery(id+"F0.wireOp",EDGE,"E182")}),-1.0]])]});
            extrude(context, id + "F1", {"entities" : qUnion([Q0]), "depth" : 6 * mm});
        }
        {
            var Q0;
            Q0=makeQuery(id+"F1.opExtrude","CAP_FACE",FACE,{"disambiguationData":[OSD([sQuery(id+"F0.wireOp",EDGE,"E182"),sQuery(id+"F0.wireOp",EDGE,"E183"),sQuery(id+"F0.wireOp",EDGE,"E184"),sQuery(id+"F0.wireOp",EDGE,"E185"),sQuery(id+"F0.wireOp",EDGE,"E186"),sQuery(id+"F0.wireOp",EDGE,"E187"),sQuery(id+"F0.wireOp",EDGE,"E188"),sQuery(id+"F0.wireOp",EDGE,"E189"),sQuery(id+"F0.wireOp",EDGE,"E190"),sQuery(id+"F0.wireOp",EDGE,"E191"),sQuery(id+"F0.wireOp",EDGE,"E192"),sQuery(id+"F0.wireOp",EDGE,"E193"),sQuery(id+"F0.wireOp",EDGE,"E194"),sQuery(id+"F0.wireOp",EDGE,"E195"),sQuery(id+"F0.wireOp",EDGE,"E196"),sQuery(id+"F0.wireOp",EDGE,"E197"),sQuery(id+"F0.wireOp",EDGE,"E198"),sQuery(id+"F0.wireOp",EDGE,"E199"),sQuery(id+"F0.wireOp",EDGE,"E200"),sQuery(id+"F0.wireOp",EDGE,"E201"),sQuery(id+"F0.wireOp",EDGE,"E202"),sQuery(id+"F0.wireOp",EDGE,"E203"),sQuery(id+"F0.wireOp",EDGE,"E204"),sQuery(id+"F0.wireOp",EDGE,"E205"),sQuery(id+"F0.wireOp",EDGE,"E206"),sQuery(id+"F0.wireOp",EDGE,"E207"),sQuery(id+"F0.wireOp",EDGE,"E208"),sQuery(id+"F0.wireOp",EDGE,"E209"),sQuery(id+"F0.wireOp",EDGE,"E210"),sQuery(id+"F0.wireOp",EDGE,"E211"),sQuery(id+"F0.wireOp",EDGE,"E212"),sQuery(id+"F0.wireOp",EDGE,"E213"),sQuery(id+"F0.wireOp",EDGE,"E214"),sQuery(id+"F0.wireOp",EDGE,"E215"),sQuery(id+"F0.wireOp",EDGE,"E216"),sQuery(id+"F0.wireOp",EDGE,"E217"),sQuery(id+"F0.wireOp",EDGE,"E218"),sQuery(id+"F0.wireOp",EDGE,"E219"),sQuery(id+"F0.wireOp",EDGE,"E220"),sQuery(id+"F0.wireOp",EDGE,"E221"),sQuery(id+"F0.wireOp",EDGE,"E222"),sQuery(id+"F0.wireOp",EDGE,"E223"),sQuery(id+"F0.wireOp",EDGE,"E224"),sQuery(id+"F0.wireOp",EDGE,"E225"),sQuery(id+"F0.wireOp",EDGE,"E226"),sQuery(id+"F0.wireOp",EDGE,"E227"),sQuery(id+"F0.wireOp",EDGE,"E228"),sQuery(id+"F0.wireOp",EDGE,"E229"),sQuery(id+"F0.wireOp",EDGE,"E230"),sQuery(id+"F0.wireOp",EDGE,"E231"),sQuery(id+"F0.wireOp",EDGE,"E232"),sQuery(id+"F0.wireOp",EDGE,"E240"),sQuery(id+"F0.wireOp",EDGE,"E241"),sQuery(id+"F0.wireOp",EDGE,"E242"),sQuery(id+"F0.wireOp",EDGE,"E243"),sQuery(id+"F0.wireOp",EDGE,"E244"),sQuery(id+"F0.wireOp",EDGE,"E245"),sQuery(id+"F0.wireOp",EDGE,"E246"),sQuery(id+"F0.wireOp",EDGE,"E247"),sQuery(id+"F0.wireOp",EDGE,"E248"),sQuery(id+"F0.wireOp",EDGE,"E249"),sQuery(id+"F0.wireOp",EDGE,"E253"),sQuery(id+"F0.wireOp",EDGE,"E254"),sQuery(id+"F0.wireOp",EDGE,"E255"),sQuery(id+"F0.wireOp",EDGE,"E256"),sQuery(id+"F0.wireOp",EDGE,"E259"),sQuery(id+"F0.wireOp",EDGE,"E260"),sQuery(id+"F0.wireOp",EDGE,"E261"),sQuery(id+"F0.wireOp",EDGE,"E262"),sQuery(id+"F0.wireOp",EDGE,"E268"),sQuery(id+"F0.wireOp",EDGE,"E269"),sQuery(id+"F0.wireOp",EDGE,"E270"),sQuery(id+"F0.wireOp",EDGE,"E271"),sQuery(id+"F0.wireOp",EDGE,"E272"),sQuery(id+"F0.wireOp",EDGE,"E273"),sQuery(id+"F0.wireOp",EDGE,"E274"),sQuery(id+"F0.wireOp",EDGE,"E275"),sQuery(id+"F0.wireOp",EDGE,"E276"),sQuery(id+"F0.wireOp",EDGE,"E278"),sQuery(id+"F0.wireOp",EDGE,"E279"),sQuery(id+"F0.wireOp",EDGE,"E280"),sQuery(id+"F0.wireOp",EDGE,"E283"),sQuery(id+"F0.wireOp",EDGE,"E284"),sQuery(id+"F0.wireOp",EDGE,"E285"),sQuery(id+"F0.wireOp",EDGE,"E286"),sQuery(id+"F0.wireOp",EDGE,"E287"),sQuery(id+"F0.wireOp",EDGE,"E288"),sQuery(id+"F0.wireOp",EDGE,"E289"),sQuery(id+"F0.wireOp",EDGE,"E290"),sQuery(id+"F0.wireOp",EDGE,"E291"),sQuery(id+"F0.wireOp",EDGE,"E292"),sQuery(id+"F0.wireOp",EDGE,"E293"),sQuery(id+"F0.wireOp",EDGE,"E294"),sQuery(id+"F0.wireOp",EDGE,"E295"),sQuery(id+"F0.wireOp",EDGE,"E296"),sQuery(id+"F0.wireOp",EDGE,"E297"),sQuery(id+"F0.wireOp",EDGE,"E298"),sQuery(id+"F0.wireOp",EDGE,"E299"),sQuery(id+"F0.wireOp",EDGE,"E300"),sQuery(id+"F0.wireOp",EDGE,"E301"),sQuery(id+"F0.wireOp",EDGE,"E302"),sQuery(id+"F0.wireOp",EDGE,"E303"),sQuery(id+"F0.wireOp",EDGE,"E304"),sQuery(id+"F0.wireOp",EDGE,"E305"),sQuery(id+"F0.wireOp",EDGE,"E306"),sQuery(id+"F0.wireOp",EDGE,"E307"),sQuery(id+"F0.wireOp",EDGE,"E308"),sQuery(id+"F0.wireOp",EDGE,"E309"),sQuery(id+"F0.wireOp",EDGE,"E310"),sQuery(id+"F0.wireOp",EDGE,"E311"),sQuery(id+"F0.wireOp",EDGE,"E318"),sQuery(id+"F0.wireOp",EDGE,"E319"),sQuery(id+"F0.wireOp",EDGE,"E320"),sQuery(id+"F0.wireOp",EDGE,"E321"),sQuery(id+"F0.wireOp",EDGE,"E322"),sQuery(id+"F0.wireOp",EDGE,"E323"),sQuery(id+"F0.wireOp",EDGE,"E324"),sQuery(id+"F0.wireOp",EDGE,"E325"),sQuery(id+"F0.wireOp",EDGE,"E329"),sQuery(id+"F0.wireOp",EDGE,"E330"),sQuery(id+"F0.wireOp",EDGE,"E331"),sQuery(id+"F0.wireOp",EDGE,"E332"),sQuery(id+"F0.wireOp",EDGE,"E333"),sQuery(id+"F0.wireOp",EDGE,"E334"),sQuery(id+"F0.wireOp",EDGE,"E335"),sQuery(id+"F0.wireOp",EDGE,"E336"),sQuery(id+"F0.wireOp",EDGE,"E337"),sQuery(id+"F0.wireOp",EDGE,"E338"),sQuery(id+"F0.wireOp",EDGE,"E349"),sQuery(id+"F0.wireOp",EDGE,"E350"),sQuery(id+"F0.wireOp",EDGE,"E351"),sQuery(id+"F0.wireOp",EDGE,"E352"),sQuery(id+"F0.wireOp",EDGE,"E353"),sQuery(id+"F0.wireOp",EDGE,"E354"),sQuery(id+"F0.wireOp",EDGE,"E355"),sQuery(id+"F0.wireOp",EDGE,"E356"),sQuery(id+"F0.wireOp",EDGE,"E357"),sQuery(id+"F0.wireOp",EDGE,"E358"),sQuery(id+"F0.wireOp",EDGE,"E359"),sQuery(id+"F0.wireOp",EDGE,"E360"),sQuery(id+"F0.wireOp",EDGE,"E361"),sQuery(id+"F0.wireOp",EDGE,"E362"),sQuery(id+"F0.wireOp",EDGE,"E363"),sQuery(id+"F0.wireOp",EDGE,"E364"),sQuery(id+"F0.wireOp",EDGE,"E373"),sQuery(id+"F0.wireOp",EDGE,"E374"),sQuery(id+"F0.wireOp",EDGE,"E375"),sQuery(id+"F0.wireOp",EDGE,"E376"),sQuery(id+"F0.wireOp",EDGE,"E377"),sQuery(id+"F0.wireOp",EDGE,"E378"),sQuery(id+"F0.wireOp",EDGE,"E379"),sQuery(id+"F0.wireOp",EDGE,"E380"),sQuery(id+"F0.wireOp",EDGE,"E381"),sQuery(id+"F0.wireOp",EDGE,"E382"),sQuery(id+"F0.wireOp",EDGE,"E383"),sQuery(id+"F0.wireOp",EDGE,"E384"),sQuery(id+"F0.wireOp",EDGE,"E385"),sQuery(id+"F0.wireOp",EDGE,"E386"),sQuery(id+"F0.wireOp",EDGE,"E387"),sQuery(id+"F0.wireOp",EDGE,"E388"),sQuery(id+"F0.wireOp",EDGE,"E389"),sQuery(id+"F0.wireOp",EDGE,"E390"),sQuery(id+"F0.wireOp",EDGE,"E391"),sQuery(id+"F0.wireOp",EDGE,"E392"),sQuery(id+"F0.wireOp",EDGE,"E393"),sQuery(id+"F0.wireOp",EDGE,"E394"),sQuery(id+"F0.wireOp",EDGE,"E395"),sQuery(id+"F0.wireOp",EDGE,"E396"),sQuery(id+"F0.wireOp",EDGE,"E397"),sQuery(id+"F0.wireOp",EDGE,"E398"),sQuery(id+"F0.wireOp",EDGE,"E399"),sQuery(id+"F0.wireOp",EDGE,"E400"),sQuery(id+"F0.wireOp",EDGE,"E401"),sQuery(id+"F0.wireOp",EDGE,"E402"),sQuery(id+"F0.wireOp",EDGE,"E403"),sQuery(id+"F0.wireOp",EDGE,"E404"),sQuery(id+"F0.wireOp",EDGE,"E405"),sQuery(id+"F0.wireOp",EDGE,"E406"),sQuery(id+"F0.wireOp",EDGE,"E407"),sQuery(id+"F0.wireOp",EDGE,"E408"),sQuery(id+"F0.wireOp",EDGE,"E409"),sQuery(id+"F0.wireOp",EDGE,"E410"),sQuery(id+"F0.wireOp",EDGE,"E411"),sQuery(id+"F0.wireOp",EDGE,"E412"),sQuery(id+"F0.wireOp",EDGE,"E413"),sQuery(id+"F0.wireOp",EDGE,"E414"),sQuery(id+"F0.wireOp",EDGE,"E415"),sQuery(id+"F0.wireOp",EDGE,"E416"),sQuery(id+"F0.wireOp",EDGE,"E417"),sQuery(id+"F0.wireOp",EDGE,"E418"),sQuery(id+"F0.wireOp",EDGE,"E419"),sQuery(id+"F0.wireOp",EDGE,"E420"),sQuery(id+"F0.wireOp",EDGE,"E421"),sQuery(id+"F0.wireOp",EDGE,"E422"),sQuery(id+"F0.wireOp",EDGE,"E423"),sQuery(id+"F0.wireOp",EDGE,"E424"),sQuery(id+"F0.wireOp",EDGE,"E425"),sQuery(id+"F0.wireOp",EDGE,"E426"),sQuery(id+"F0.wireOp",EDGE,"E427"),sQuery(id+"F0.wireOp",EDGE,"E428"),sQuery(id+"F0.wireOp",EDGE,"E429"),sQuery(id+"F0.wireOp",EDGE,"E430"),sQuery(id+"F0.wireOp",EDGE,"E431"),sQuery(id+"F0.wireOp",EDGE,"E432"),sQuery(id+"F0.wireOp",EDGE,"E433"),sQuery(id+"F0.wireOp",EDGE,"E434"),sQuery(id+"F0.wireOp",EDGE,"E435"),sQuery(id+"F0.wireOp",EDGE,"E436"),sQuery(id+"F0.wireOp",EDGE,"E437"),sQuery(id+"F0.wireOp",EDGE,"E438"),sQuery(id+"F0.wireOp",EDGE,"E439"),sQuery(id+"F0.wireOp",EDGE,"E440"),sQuery(id+"F0.wireOp",EDGE,"E441"),sQuery(id+"F0.wireOp",EDGE,"E442"),sQuery(id+"F0.wireOp",EDGE,"E443"),sQuery(id+"F0.wireOp",EDGE,"E444"),sQuery(id+"F0.wireOp",EDGE,"E445"),sQuery(id+"F0.wireOp",EDGE,"E446"),sQuery(id+"F0.wireOp",EDGE,"E447"),sQuery(id+"F0.wireOp",EDGE,"E448"),sQuery(id+"F0.wireOp",EDGE,"E449"),sQuery(id+"F0.wireOp",EDGE,"E450"),sQuery(id+"F0.wireOp",EDGE,"E451"),sQuery(id+"F0.wireOp",EDGE,"E452"),sQuery(id+"F0.wireOp",EDGE,"E453"),sQuery(id+"F0.wireOp",EDGE,"E454"),sQuery(id+"F0.wireOp",EDGE,"E455"),sQuery(id+"F0.wireOp",EDGE,"E456"),sQuery(id+"F0.wireOp",EDGE,"E457"),sQuery(id+"F0.wireOp",EDGE,"E459"),sQuery(id+"F0.wireOp",EDGE,"E460"),sQuery(id+"F0.wireOp",EDGE,"E461")])],"isStart":true});
            var sketch = newSketch(context, id + "F2", { "sketchPlane" : qUnion([Q0])});
            skCircle(sketch, "E463", {"center": v(0.95, -24.4) * mm, "radius": 10.14 * mm});
            skSolve(sketch);
        }
        {
            var Q0;
            Q0=makeQuery(id+"F2.imprint","IMPRINT",FACE,{"disambiguationData":[TD([[makeQuery(id+"F2.imprint","IMPRINT",EDGE,{"derivedFrom":sQuery(id+"F2.wireOp",EDGE,"E463")}),1.0]])]});
            extrude(context, id + "F3", {"entities" : qUnion([Q0]), "operationType" : NewBodyOperationType.REMOVE, "oppositeDirection" : true, "depth" : 3.25 * mm});
        }
    });
